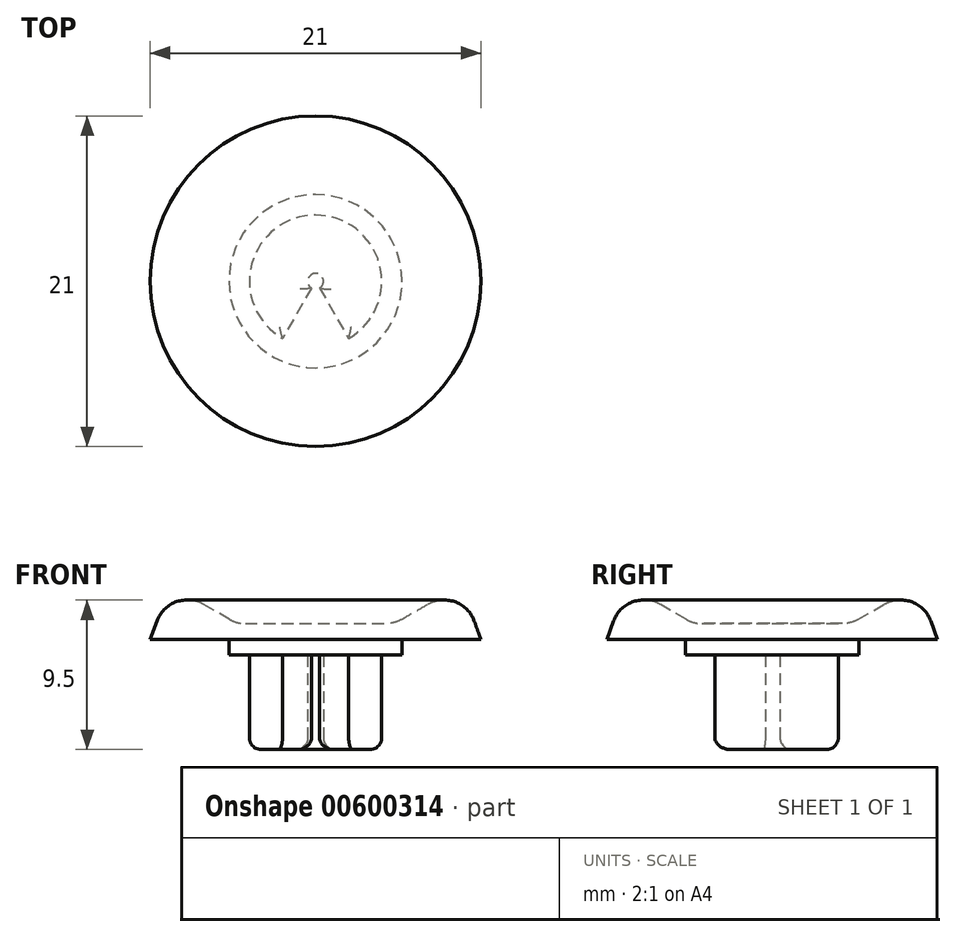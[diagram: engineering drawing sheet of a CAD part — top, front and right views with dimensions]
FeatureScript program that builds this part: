
annotation { "Feature Type Name" : "Feature", "Feature Type Description" : "" }
export const myFeature = defineFeature(function(context is Context, id is Id, definition is map)
    precondition{}
    {
        {
            var Q0;
            Q0=qCreatedBy(makeId("Front.planeOp"),FACE);
            var sketch = newSketch(context, id + "F0", { "sketchPlane" : qUnion([Q0])});
            skLineSegment(sketch, "E0", {"start": v(5.5, 6) * mm, "end": v(5.5, 7) * mm});
            skLineSegment(sketch, "E1", {"start": v(5.5, 7) * mm, "end": v(10.5, 7) * mm});
            skLineSegment(sketch, "E2", {"start": v(0, 8) * mm, "end": v(0, 0) * mm});
            skLineSegment(sketch, "E3", {"start": v(5.5, 6) * mm, "end": v(4.2, 6) * mm});
            skLineSegment(sketch, "E4", {"start": v(4.2, 6) * mm, "end": v(4.2, 0) * mm});
            skLineSegment(sketch, "E5", {"start": v(4.2, 0) * mm, "end": v(0, 0) * mm});
            skPoint(sketch, "E6.orphan", {"position": v(0, 0) * mm});
            skLineSegment(sketch, "E7", {"start": v(10.5, 7) * mm, "end": v(9.6, 9.5) * mm});
            skLineSegment(sketch, "E8", {"start": v(9.6, 9.5) * mm, "end": v(7.6, 9.5) * mm});
            skLineSegment(sketch, "E9", {"start": v(7.6, 9.5) * mm, "end": v(5, 8) * mm});
            skLineSegment(sketch, "E10", {"start": v(5, 8) * mm, "end": v(0, 8) * mm});
            skSolve(sketch);
        }
        {
            var Q0;
            Q0=qSketchRegion(id+"F0",true);
            var Q1;
            Q1=sQuery(id+"F0.wireOp",EDGE,"E2");
            revolve(context, id + "F1", {"entities" : qUnion([Q0]), "axis" : qUnion([Q1]), "revolveType" : RevolveType.FULL});
        }
        {
            var Q0;
            Q0=makeQuery(id+"F1.opRevolve","SWEPT_FACE",FACE,{"disambiguationData":[OSD([sQuery(id+"F0.wireOp",EDGE,"E5")])]});
            var sketch = newSketch(context, id + "F2", { "sketchPlane" : qUnion([Q0])});
            skArc(sketch, "E11", {"start": v(-0.25, 0.43) * mm, "mid": v(0, -0.5) * mm, "end": v(0.25, 0.43) * mm});
            skArc(sketch, "E12.0", {"start": v(2.1, 3.64) * mm, "mid": v(0, 4.2) * mm, "end": v(-2.1, 3.64) * mm});
            skLineSegment(sketch, "E13", {"start": v(-2.1, 3.64) * mm, "end": v(-0.25, 0.43) * mm});
            skLineSegment(sketch, "E14", {"start": v(2.1, 3.64) * mm, "end": v(0.25, 0.43) * mm});
            skSolve(sketch);
        }
        {
            var Q0;
            Q0=qSketchRegion(id+"F2",true);
            var Q1;
            Q1=makeQuery(id+"F1.opRevolve","SWEPT_FACE",FACE,{"disambiguationData":[OSD([sQuery(id+"F0.wireOp",EDGE,"E3")])]});
            extrude(context, id + "F3", {"entities" : qUnion([Q0]), "operationType" : NewBodyOperationType.REMOVE, "endBound" : BoundingType.UP_TO_SURFACE, "oppositeDirection" : true, "depth" : 25 * mm, "endBoundEntityFace" : qUnion([Q1]), "offsetDistance" : 25 * mm});
        }
        {
            var Q0;
            {var subQ2=makeQuery(id+"F3.boolean.opBoolean","COPY",FACE,{"derivedFrom":makeQuery(id+"F3.opExtrude","SWEPT_FACE",FACE,{"disambiguationData":[OSD([sQuery(id+"F2.wireOp",EDGE,"E13")])]})});Q0=makeQuery(id+"Fmqv6moUgZnORJw_2.2.F3.boolean.opBoolean","SPLIT",FACE,{"disambiguationData":[TD([subQ2])],"derivedFrom":makeQuery(id+"Fmqv6moUgZnORJw_2.1.F3.boolean.opBoolean","SPLIT",FACE,{"disambiguationData":[TD([subQ2])],"derivedFrom":makeQuery(id+"F1.opRevolve","SWEPT_FACE",FACE,{"disambiguationData":[OSD([sQuery(id+"F0.wireOp",EDGE,"E5")])]})})});}
            var Q1;
            {var subQ1=makeQuery(id+"Fmqv6moUgZnORJw_2.1.F3.opExtrude","SWEPT_FACE",FACE,{"disambiguationData":[OSD([sQuery(id+"F2.wireOp",EDGE,"E14")])]});var subQ3=sQuery(id+"F2.wireOp",EDGE,"E13");Q1=makeQuery(id+"Fmqv6moUgZnORJw_2.2.F3.boolean.opBoolean","SPLIT",FACE,{"disambiguationData":[TD([makeQuery(id+"Fmqv6moUgZnORJw_2.1.F3.boolean.opBoolean","COPY",FACE,{"derivedFrom":subQ1})])],"derivedFrom":makeQuery(id+"Fmqv6moUgZnORJw_2.1.F3.boolean.opBoolean","SPLIT",FACE,{"disambiguationData":[TD([makeQuery(id+"F3.boolean.opBoolean","COPY",FACE,{"derivedFrom":makeQuery(id+"F3.opExtrude","SWEPT_FACE",FACE,{"disambiguationData":[OSD([subQ3])]})})])],"derivedFrom":makeQuery(id+"F1.opRevolve","SWEPT_FACE",FACE,{"disambiguationData":[OSD([sQuery(id+"F0.wireOp",EDGE,"E5")])]})})});}
            var Q2;
            Q2=makeQuery(id+"Fmqv6moUgZnORJw_2.1.F3.boolean.opBoolean","SPLIT",FACE,{"disambiguationData":[TD([makeQuery(id+"F3.boolean.opBoolean","COPY",FACE,{"derivedFrom":makeQuery(id+"F3.opExtrude","SWEPT_FACE",FACE,{"disambiguationData":[OSD([sQuery(id+"F2.wireOp",EDGE,"E14")])]})})])],"derivedFrom":makeQuery(id+"F1.opRevolve","SWEPT_FACE",FACE,{"disambiguationData":[OSD([sQuery(id+"F0.wireOp",EDGE,"E5")])]})});
            fillet(context, id + "F4", {"entities" : qUnion([Q0, Q1, Q2]), "radius" : .75 * mm, "tangentPropagation" : true, "allowEdgeOverflow" : false});
        }
        {
            var Q0;
            Q0=makeQuery(id+"F1.opRevolve","SWEPT_FACE",FACE,{"disambiguationData":[OSD([sQuery(id+"F0.wireOp",EDGE,"E8")])]});
            var Q1;
            Q1=makeQuery(id+"F1.opRevolve","SWEPT_EDGE",EDGE,{"disambiguationData":[OSD([sQuery(id+"F0.wireOp",EDGE,"E9"),sQuery(id+"F0.wireOp",EDGE,"E10")])]});
            fillet(context, id + "F5", {"entities" : qUnion([Q0, Q1]), "radius" : 2 * mm, "tangentPropagation" : true, "allowEdgeOverflow" : false});
        }
    });
